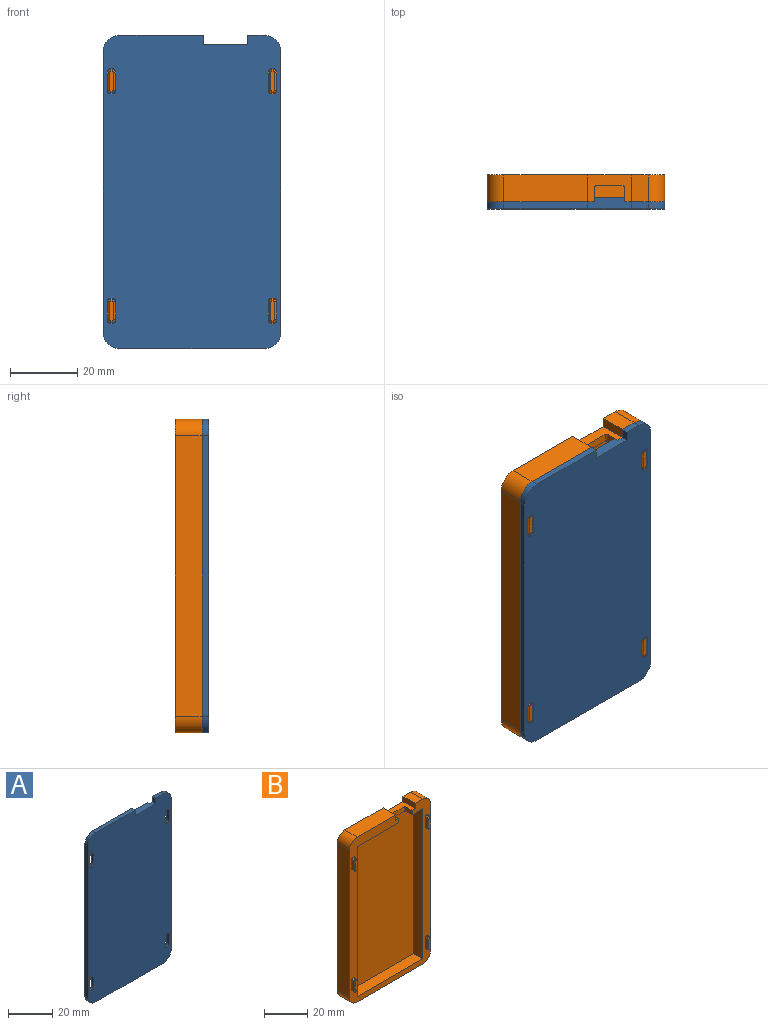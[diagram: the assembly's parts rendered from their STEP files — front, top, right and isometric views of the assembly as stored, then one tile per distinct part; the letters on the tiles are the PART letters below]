
ASSEMBLY  parts=2 mates=1
PART A: 82 faces, bbox 53x3.3x93.4 mm
  f0: plane 5.5x1.5mm, normal (-1,0,0), area 8.3mm2, adj f24,f46,f49,f55
  f1: plane 1.5x0.5mm, normal (0,0,1), area 0.8mm2, adj f24,f46,f47,f51
  f2: plane 5.5x1.5mm, normal (1,0,0), area 8.3mm2, adj f24,f47,f48,f52
  f3: plane 1.5x0.5mm, normal (0,0,-1), area 0.8mm2, adj f24,f42,f45,f64
  f4: plane 5.5x1.5mm, normal (-1,0,0), area 8.3mm2, adj f24,f42,f43,f63
  f5: plane 1.5x0.5mm, normal (0,0,1), area 0.8mm2, adj f24,f43,f44,f59
  f6: plane 5.5x1.5mm, normal (1,0,0), area 8.3mm2, adj f24,f38,f41,f77
  f7: plane 1.5x0.5mm, normal (0,0,-1), area 0.8mm2, adj f24,f38,f39,f81
  f8: plane 5.5x1.5mm, normal (-1,0,0), area 8.3mm2, adj f24,f39,f40,f78
  f9: plane 1.5x0.5mm, normal (0,0,1), area 0.8mm2, adj f24,f34,f37,f67
  f10: plane 5.5x1.5mm, normal (1,0,0), area 8.3mm2, adj f24,f34,f35,f68
  f11: plane 1.5x0.5mm, normal (0,0,-1), area 0.8mm2, adj f24,f35,f36,f72
  f12: plane 13x3.25mm, normal (0,0,1), area 37.3mm2, adj f13,f19,f24,f25,f26,f28,f29
  f13: plane 2.93x2mm, normal (1,0,0), area 5.9mm2, adj f12,f14,f24,f25
  f14: plane 25x2mm, normal (0,0,1), area 50mm2, adj f13,f24,f25,f31
  f15: plane 83.43x2mm, normal (-1,0,0), area 166.9mm2, adj f24,f25,f31,f32
  f16: plane 43x2mm, normal (0,0,-1), area 86mm2, adj f24,f25,f32,f33
  f17: plane 83.43x2mm, normal (1,0,0), area 166.9mm2, adj f24,f25,f30,f33
  f18: plane 5x2mm, normal (0,0,1), area 10mm2, adj f19,f24,f25,f30
  f19: plane 2.93x2mm, normal (-1,0,0), area 5.9mm2, adj f12,f18,f24,f25
  f20: plane 5.5x1.5mm, normal (1,0,0), area 8.3mm2, adj f24,f44,f45,f60
  f21: plane 1.5x0.5mm, normal (0,0,1), area 0.8mm2, adj f24,f40,f41,f74
  f22: plane 5.5x1.5mm, normal (-1,0,0), area 8.3mm2, adj f24,f36,f37,f71
  f23: plane 1.5x0.5mm, normal (0,0,-1), area 0.8mm2, adj f24,f48,f49,f56
  f24: plane 93.43x53mm, normal (0,-1,0), area 4820.7mm2, adj f0,f1,f2,f3,f4,f5,f6,f7
  f25: plane 93.43x53mm, normal (0,1,0), area 4758.5mm2, adj f12,f13,f14,f15,f16,f17,f18,f19
  f26: plane 2.5x1.25mm, normal (-1,0,0), area 3.1mm2, adj f12,f25,f27,f29
  f27: plane 9x1.25mm, normal (0,0,-1), area 11.3mm2, adj f25,f26,f28,f29
  f28: plane 2.5x1.25mm, normal (1,0,0), area 3.1mm2, adj f12,f25,f27,f29
  f29: plane 9x2.5mm, normal (0,1,0), area 22.5mm2, adj f12,f26,f27,f28
  f30: cylinder r=5mm len=5mm, axis (0,1,0), area 15.7mm2, adj f17,f18,f24,f25
  f31: cylinder r=5mm len=5mm, axis (0,1,0), area 15.7mm2, adj f14,f15,f24,f25
  f32: cylinder r=5mm len=5mm, axis (0,1,0), area 15.7mm2, adj f15,f16,f24,f25
  f33: cylinder r=5mm len=5mm, axis (0,-1,0), area 15.7mm2, adj f16,f17,f24,f25
  f34: cylinder r=1mm len=1.5mm, axis (0,-1,0), area 2.4mm2, adj f9,f10,f24,f66
  f35: cylinder r=1mm len=1.5mm, axis (0,1,0), area 2.4mm2, adj f10,f11,f24,f70
  f36: cylinder r=1mm len=1.5mm, axis (0,-1,0), area 2.4mm2, adj f11,f22,f24,f73
  f37: cylinder r=1mm len=1.5mm, axis (0,1,0), area 2.4mm2, adj f9,f22,f24,f69
  f38: cylinder r=1mm len=1.5mm, axis (0,-1,0), area 2.4mm2, adj f6,f7,f24,f79
  f39: cylinder r=1mm len=1.5mm, axis (0,1,0), area 2.4mm2, adj f7,f8,f24,f80
  f40: cylinder r=1mm len=1.5mm, axis (0,-1,0), area 2.4mm2, adj f8,f21,f24,f76
  f41: cylinder r=1mm len=1.5mm, axis (0,1,0), area 2.4mm2, adj f6,f21,f24,f75
  f42: cylinder r=1mm len=1.5mm, axis (0,1,0), area 2.4mm2, adj f3,f4,f24,f65
  f43: cylinder r=1mm len=1.5mm, axis (0,-1,0), area 2.4mm2, adj f4,f5,f24,f61
  f44: cylinder r=1mm len=1.5mm, axis (0,1,0), area 2.4mm2, adj f5,f20,f24,f58
  f45: cylinder r=1mm len=1.5mm, axis (0,-1,0), area 2.4mm2, adj f3,f20,f24,f62
  f46: cylinder r=1mm len=1.5mm, axis (0,1,0), area 2.4mm2, adj f0,f1,f24,f53
  f47: cylinder r=1mm len=1.5mm, axis (0,-1,0), area 2.4mm2, adj f1,f2,f24,f50
  f48: cylinder r=1mm len=1.5mm, axis (0,1,0), area 2.4mm2, adj f2,f23,f24,f54
  f49: cylinder r=1mm len=1.5mm, axis (0,-1,0), area 2.4mm2, adj f0,f23,f24,f57
  f50: torus R=1.5mm, axis (0,-1,0), area 1.5mm2, adj f25,f47,f51,f52
  f51: cylinder r=0.5mm len=0.5mm, axis (-1,0,0), area 0.4mm2, adj f1,f25,f50,f53
  f52: cylinder r=0.5mm len=5.5mm, axis (0,0,1), area 4.3mm2, adj f2,f25,f50,f54
  f53: torus R=1.5mm, axis (0,-1,0), area 1.5mm2, adj f25,f46,f51,f55
  f54: torus R=1.5mm, axis (0,-1,0), area 1.5mm2, adj f25,f48,f52,f56
  f55: cylinder r=0.5mm len=5.5mm, axis (0,0,-1), area 4.3mm2, adj f0,f25,f53,f57
  f56: cylinder r=0.5mm len=0.5mm, axis (1,0,0), area 0.4mm2, adj f23,f25,f54,f57
  f57: torus R=1.5mm, axis (0,-1,0), area 1.5mm2, adj f25,f49,f55,f56
  f58: torus R=1.5mm, axis (0,-1,0), area 1.5mm2, adj f25,f44,f59,f60
  f59: cylinder r=0.5mm len=0.5mm, axis (-1,0,0), area 0.4mm2, adj f5,f25,f58,f61
  f60: cylinder r=0.5mm len=5.5mm, axis (0,0,1), area 4.3mm2, adj f20,f25,f58,f62
  f61: torus R=1.5mm, axis (0,-1,0), area 1.5mm2, adj f25,f43,f59,f63
  f62: torus R=1.5mm, axis (0,-1,0), area 1.5mm2, adj f25,f45,f60,f64
  f63: cylinder r=0.5mm len=5.5mm, axis (0,0,-1), area 4.3mm2, adj f4,f25,f61,f65
  f64: cylinder r=0.5mm len=0.5mm, axis (1,0,0), area 0.4mm2, adj f3,f25,f62,f65
  f65: torus R=1.5mm, axis (0,-1,0), area 1.5mm2, adj f25,f42,f63,f64
  f66: torus R=1.5mm, axis (0,-1,0), area 1.5mm2, adj f25,f34,f67,f68
  f67: cylinder r=0.5mm len=0.5mm, axis (-1,0,0), area 0.4mm2, adj f9,f25,f66,f69
  f68: cylinder r=0.5mm len=5.5mm, axis (0,0,1), area 4.3mm2, adj f10,f25,f66,f70
  f69: torus R=1.5mm, axis (0,-1,0), area 1.5mm2, adj f25,f37,f67,f71
  f70: torus R=1.5mm, axis (0,-1,0), area 1.5mm2, adj f25,f35,f68,f72
  f71: cylinder r=0.5mm len=5.5mm, axis (0,0,-1), area 4.3mm2, adj f22,f25,f69,f73
  f72: cylinder r=0.5mm len=0.5mm, axis (1,0,0), area 0.4mm2, adj f11,f25,f70,f73
  f73: torus R=1.5mm, axis (0,-1,0), area 1.5mm2, adj f25,f36,f71,f72
  f74: cylinder r=0.5mm len=0.5mm, axis (-1,0,0), area 0.4mm2, adj f21,f25,f75,f76
  f75: torus R=1.5mm, axis (0,-1,0), area 1.5mm2, adj f25,f41,f74,f77
  f76: torus R=1.5mm, axis (0,-1,0), area 1.5mm2, adj f25,f40,f74,f78
  f77: cylinder r=0.5mm len=5.5mm, axis (0,0,1), area 4.3mm2, adj f6,f25,f75,f79
  f78: cylinder r=0.5mm len=5.5mm, axis (0,0,-1), area 4.3mm2, adj f8,f25,f76,f80
  f79: torus R=1.5mm, axis (0,-1,0), area 1.5mm2, adj f25,f38,f77,f81
  f80: torus R=1.5mm, axis (0,-1,0), area 1.5mm2, adj f25,f39,f78,f81
  f81: cylinder r=0.5mm len=0.5mm, axis (1,0,0), area 0.4mm2, adj f7,f25,f79,f80
PART B: 92 faces, bbox 53x10x93.4 mm
  f0: plane 85x43mm, normal (0,-1,0), area 3655mm2, adj f2,f3,f4,f5
  f1: plane 93.43x53mm, normal (0,1,0), area 4892.2mm2, adj f7,f8,f9,f10,f11,f12,f13,f14
  f2: plane 85x6mm, normal (1,0,0), area 510mm2, adj f0,f3,f5,f16
  f3: plane 43x6mm, normal (0,0,1), area 258mm2, adj f0,f2,f4,f16
  f4: plane 85x6mm, normal (-1,0,0), area 510mm2, adj f0,f3,f5,f16
  f5: plane 43x6mm, normal (0,0,-1), area 215.4mm2, adj f0,f2,f4,f6,f15,f16,f17,f58
  f6: plane 4.25x2.5mm, normal (1,0,0), area 10.6mm2, adj f5,f7,f16,f59
  f7: plane 13x8mm, normal (0,0,1), area 61.4mm2, adj f1,f6,f8,f14,f15,f16,f17,f58
  f8: plane 8x2.93mm, normal (1,0,0), area 23.4mm2, adj f1,f7,f9,f16
  f9: plane 25x8mm, normal (0,0,1), area 200mm2, adj f1,f8,f16,f39
  f10: plane 83.43x8mm, normal (-1,0,0), area 667.4mm2, adj f1,f16,f39,f40
  f11: plane 43x8mm, normal (0,0,-1), area 344mm2, adj f1,f16,f40,f41
  f12: plane 83.43x8mm, normal (1,0,0), area 667.4mm2, adj f1,f16,f38,f41
  f13: plane 8x5mm, normal (0,0,1), area 40mm2, adj f1,f14,f16,f38
  f14: plane 8x2.93mm, normal (-1,0,0), area 23.4mm2, adj f1,f7,f13,f16
  f15: plane 4.25x2.5mm, normal (-1,0,0), area 10.6mm2, adj f5,f7,f16,f58
  f16: plane 93.43x53mm, normal (0,-1,0), area 1160.9mm2, adj f2,f3,f4,f5,f6,f7,f8,f9
  f17: plane 8x2.5mm, normal (0,-1,0), area 20mm2, adj f5,f7,f58,f59
  f18: plane 6x1mm, normal (0,-1,0), area 5.9mm2, adj f76,f77,f78,f79,f80,f81,f82,f83
  f19: plane 5.4x1.5mm, normal (-1,0,0), area 8.1mm2, adj f16,f46,f47,f81
  f20: plane 1.5x0.4mm, normal (0,0,1), area 0.6mm2, adj f16,f47,f48,f77
  f21: plane 5.4x1.5mm, normal (1,0,0), area 8.1mm2, adj f16,f48,f49,f78
  f22: plane 1.5x0.4mm, normal (0,0,-1), area 0.6mm2, adj f16,f46,f49,f82
  f23: plane 6x1mm, normal (0,-1,0), area 5.9mm2, adj f84,f85,f86,f87,f88,f89,f90,f91
  f24: plane 5.4x1.5mm, normal (1,0,0), area 8.1mm2, adj f16,f42,f43,f89
  f25: plane 1.5x0.4mm, normal (0,0,-1), area 0.6mm2, adj f16,f43,f44,f85
  f26: plane 5.4x1.5mm, normal (-1,0,0), area 8.1mm2, adj f16,f44,f45,f86
  f27: plane 1.5x0.4mm, normal (0,0,1), area 0.6mm2, adj f16,f42,f45,f90
  f28: plane 6x1mm, normal (0,-1,0), area 5.9mm2, adj f60,f61,f62,f63,f64,f65,f66,f67
  f29: plane 1.5x0.4mm, normal (0,0,-1), area 0.6mm2, adj f16,f54,f55,f65
  f30: plane 5.4x1.5mm, normal (-1,0,0), area 8.1mm2, adj f16,f55,f56,f61
  f31: plane 1.5x0.4mm, normal (0,0,1), area 0.6mm2, adj f16,f56,f57,f62
  f32: plane 5.4x1.5mm, normal (1,0,0), area 8.1mm2, adj f16,f54,f57,f66
  f33: plane 6x1mm, normal (0,-1,0), area 5.9mm2, adj f68,f69,f70,f71,f72,f73,f74,f75
  f34: plane 1.5x0.4mm, normal (0,0,1), area 0.6mm2, adj f16,f52,f53,f69
  f35: plane 5.4x1.5mm, normal (1,0,0), area 8.1mm2, adj f16,f51,f52,f70
  f36: plane 1.5x0.4mm, normal (0,0,-1), area 0.6mm2, adj f16,f50,f51,f74
  f37: plane 5.4x1.5mm, normal (-1,0,0), area 8.1mm2, adj f16,f50,f53,f73
  f38: cylinder r=5mm len=8mm, axis (0,1,0), area 62.8mm2, adj f1,f12,f13,f16
  f39: cylinder r=5mm len=8mm, axis (0,1,0), area 62.8mm2, adj f1,f9,f10,f16
  f40: cylinder r=5mm len=8mm, axis (0,1,0), area 62.8mm2, adj f1,f10,f11,f16
  f41: cylinder r=5mm len=8mm, axis (0,-1,0), area 62.8mm2, adj f1,f11,f12,f16
  f42: cylinder r=0.8mm len=1.5mm, axis (0,-1,0), area 1.9mm2, adj f16,f24,f27,f91
  f43: cylinder r=0.8mm len=1.5mm, axis (0,1,0), area 1.9mm2, adj f16,f24,f25,f87
  f44: cylinder r=0.8mm len=1.5mm, axis (0,-1,0), area 1.9mm2, adj f16,f25,f26,f84
  f45: cylinder r=0.8mm len=1.5mm, axis (0,1,0), area 1.9mm2, adj f16,f26,f27,f88
  f46: cylinder r=0.8mm len=1.5mm, axis (0,1,0), area 1.9mm2, adj f16,f19,f22,f83
  f47: cylinder r=0.8mm len=1.5mm, axis (0,-1,0), area 1.9mm2, adj f16,f19,f20,f79
  f48: cylinder r=0.8mm len=1.5mm, axis (0,1,0), area 1.9mm2, adj f16,f20,f21,f76
  f49: cylinder r=0.8mm len=1.5mm, axis (0,-1,0), area 1.9mm2, adj f16,f21,f22,f80
  f50: cylinder r=0.8mm len=1.5mm, axis (0,1,0), area 1.9mm2, adj f16,f36,f37,f75
  f51: cylinder r=0.8mm len=1.5mm, axis (0,-1,0), area 1.9mm2, adj f16,f35,f36,f72
  f52: cylinder r=0.8mm len=1.5mm, axis (0,1,0), area 1.9mm2, adj f16,f34,f35,f68
  f53: cylinder r=0.8mm len=1.5mm, axis (0,-1,0), area 1.9mm2, adj f16,f34,f37,f71
  f54: cylinder r=0.8mm len=1.5mm, axis (0,1,0), area 1.9mm2, adj f16,f29,f32,f67
  f55: cylinder r=0.8mm len=1.5mm, axis (0,-1,0), area 1.9mm2, adj f16,f29,f30,f63
  f56: cylinder r=0.8mm len=1.5mm, axis (0,1,0), area 1.9mm2, adj f16,f30,f31,f60
  f57: cylinder r=0.8mm len=1.5mm, axis (0,-1,0), area 1.9mm2, adj f16,f31,f32,f64
  f58: cylinder r=0.5mm len=2.5mm, axis (0,0,-1), area 2mm2, adj f5,f7,f15,f17
  f59: cylinder r=0.5mm len=2.5mm, axis (0,0,1), area 2mm2, adj f5,f6,f7,f17
  f60: torus R=0.3mm, axis (0,-1,0), area 0.8mm2, adj f28,f56,f61,f62
  f61: cylinder r=0.5mm len=5.4mm, axis (0,0,1), area 4.2mm2, adj f28,f30,f60,f63
  f62: cylinder r=0.5mm len=0.5mm, axis (1,0,0), area 0.3mm2, adj f28,f31,f60,f64
  f63: torus R=0.3mm, axis (0,-1,0), area 0.8mm2, adj f28,f55,f61,f65
  f64: torus R=0.3mm, axis (0,-1,0), area 0.8mm2, adj f28,f57,f62,f66
  f65: cylinder r=0.5mm len=0.5mm, axis (-1,0,0), area 0.3mm2, adj f28,f29,f63,f67
  f66: cylinder r=0.5mm len=5.4mm, axis (0,0,-1), area 4.2mm2, adj f28,f32,f64,f67
  f67: torus R=0.3mm, axis (0,-1,0), area 0.8mm2, adj f28,f54,f65,f66
  f68: torus R=0.3mm, axis (0,-1,0), area 0.8mm2, adj f33,f52,f69,f70
  f69: cylinder r=0.5mm len=0.5mm, axis (1,0,0), area 0.3mm2, adj f33,f34,f68,f71
  f70: cylinder r=0.5mm len=5.4mm, axis (0,0,-1), area 4.2mm2, adj f33,f35,f68,f72
  f71: torus R=0.3mm, axis (0,-1,0), area 0.8mm2, adj f33,f53,f69,f73
  f72: torus R=0.3mm, axis (0,-1,0), area 0.8mm2, adj f33,f51,f70,f74
  f73: cylinder r=0.5mm len=5.4mm, axis (0,0,1), area 4.2mm2, adj f33,f37,f71,f75
  f74: cylinder r=0.5mm len=0.5mm, axis (-1,0,0), area 0.3mm2, adj f33,f36,f72,f75
  f75: torus R=0.3mm, axis (0,-1,0), area 0.8mm2, adj f33,f50,f73,f74
  f76: torus R=0.3mm, axis (0,-1,0), area 0.8mm2, adj f18,f48,f77,f78
  f77: cylinder r=0.5mm len=0.5mm, axis (1,0,0), area 0.3mm2, adj f18,f20,f76,f79
  f78: cylinder r=0.5mm len=5.4mm, axis (0,0,-1), area 4.2mm2, adj f18,f21,f76,f80
  f79: torus R=0.3mm, axis (0,-1,0), area 0.8mm2, adj f18,f47,f77,f81
  f80: torus R=0.3mm, axis (0,-1,0), area 0.8mm2, adj f18,f49,f78,f82
  f81: cylinder r=0.5mm len=5.4mm, axis (0,0,1), area 4.2mm2, adj f18,f19,f79,f83
  f82: cylinder r=0.5mm len=0.5mm, axis (-1,0,0), area 0.3mm2, adj f18,f22,f80,f83
  f83: torus R=0.3mm, axis (0,-1,0), area 0.8mm2, adj f18,f46,f81,f82
  f84: torus R=0.3mm, axis (0,-1,0), area 0.8mm2, adj f23,f44,f85,f86
  f85: cylinder r=0.5mm len=0.5mm, axis (-1,0,0), area 0.3mm2, adj f23,f25,f84,f87
  f86: cylinder r=0.5mm len=5.4mm, axis (0,0,1), area 4.2mm2, adj f23,f26,f84,f88
  f87: torus R=0.3mm, axis (0,-1,0), area 0.8mm2, adj f23,f43,f85,f89
  f88: torus R=0.3mm, axis (0,-1,0), area 0.8mm2, adj f23,f45,f86,f90
  f89: cylinder r=0.5mm len=5.4mm, axis (0,0,-1), area 4.2mm2, adj f23,f24,f87,f91
  f90: cylinder r=0.5mm len=0.5mm, axis (1,0,0), area 0.3mm2, adj f23,f27,f88,f91
  f91: torus R=0.3mm, axis (0,-1,0), area 0.8mm2, adj f23,f42,f89,f90
PLACE A t=(-0.39,0.43,-1.04)mm
PLACE B t=(-0.39,8.43,-1.04)mm
MATE parallel A.f31 <-> B.f39  axis (0,1,0) through (-21.89,0.43,41.89)mm
